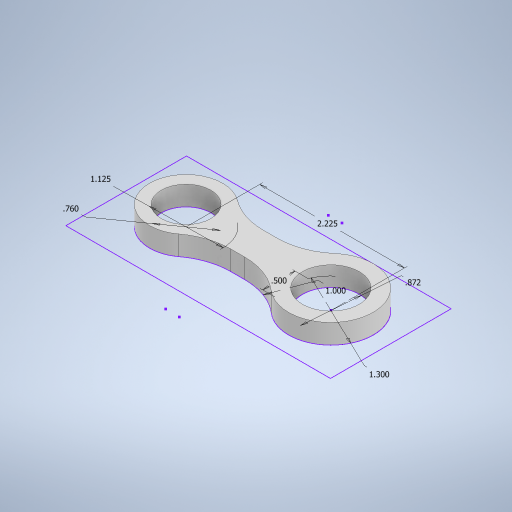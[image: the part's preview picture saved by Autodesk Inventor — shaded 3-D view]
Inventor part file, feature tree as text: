
AUTODESK INVENTOR PART (.ipt)
format: ipt  version: 2023 (Build 270158000, 158)  size: 286,208 bytes
history: native  units: in
note: dims shown in document units (in); Inventor stores cm internally (conversion verified against a paired STEP export)
features: extrude x1, sketch x1
ambient origin geometry x8: Origin, YZ Plane, XZ Plane, XY Plane, X Axis, Y Axis, Z Axis, Center Point
bodies: Body1 (feature_tree)
feature tree (2):
  extrude  "Extrusion2"  Depth=0.5in
  sketch  "Sketch1"  dims[d15=0.872in d17=0.5in d18=1.3in d19=0.76in d20=1.125in d21=2.225in d22=0.3in d23=0.0in d35=1.0in d3=0.5in d4=0.0344in d5=0.5in d6=0.0344in d28=0.0in d29=0.0in d30=0.0in d31=0.0in d36=0.0344in d37=0.5in d38=0.0344in]
